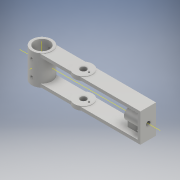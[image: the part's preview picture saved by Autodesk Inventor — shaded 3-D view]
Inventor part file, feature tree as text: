
AUTODESK INVENTOR PART (.ipt)
format: ipt  version: 2017 (Build 210142000, 142)  size: 251,392 bytes
history: native  units: mm
features: sketch x11, extrude x7, hole x4, mirror x3, other x1
ambient origin geometry x8: Origin, YZ Plane, XZ Plane, XY Plane, X Axis, Y Axis, Z Axis, Center Point
bodies: Solide1 (feature_tree)
feature tree (26):
  extrude  "Extrusion1"  Depth=40.0mm
  other  "Plan de construction1"
  extrude  "Extrusion2"  Depth=30.0mm
  extrude  "Extrusion3"  Depth=59.0mm TaperAngle=0.0deg
  extrude  "Extrusion4"  [1 undecoded]
  hole  "Perçage1"  [1 undecoded]
  mirror  "Symétrie1"
  extrude  "Extrusion5"  Depth=15.5mm
  extrude  "Extrusion6"  Depth=6.0mm TaperAngle=0.0deg
  hole  "Perçage2"  [1 undecoded]
  mirror  "Symétrie2"
  extrude  "Extrusion7"  Depth=82.0mm
  hole  "Perçage3"  [1 undecoded]
  hole  "Perçage4"  [1 undecoded]
  mirror  "Symétrie3"
  sketch  "Esquisse1"
  sketch  "Esquisse2"
  sketch  "Esquisse3"
  sketch  "Esquisse4"
  sketch  "Esquisse5"
  sketch  "Esquisse6"
  sketch  "Esquisse8"
  sketch  "Esquisse9"
  sketch  "Esquisse10"
  sketch  "Esquisse11"
  sketch  "Esquisse12"
note: 5 required parameter values undecoded (feature->parameter linkage not recoverable at this tier; creation-order binding heuristic only, values carry confidence <= 0.55)
